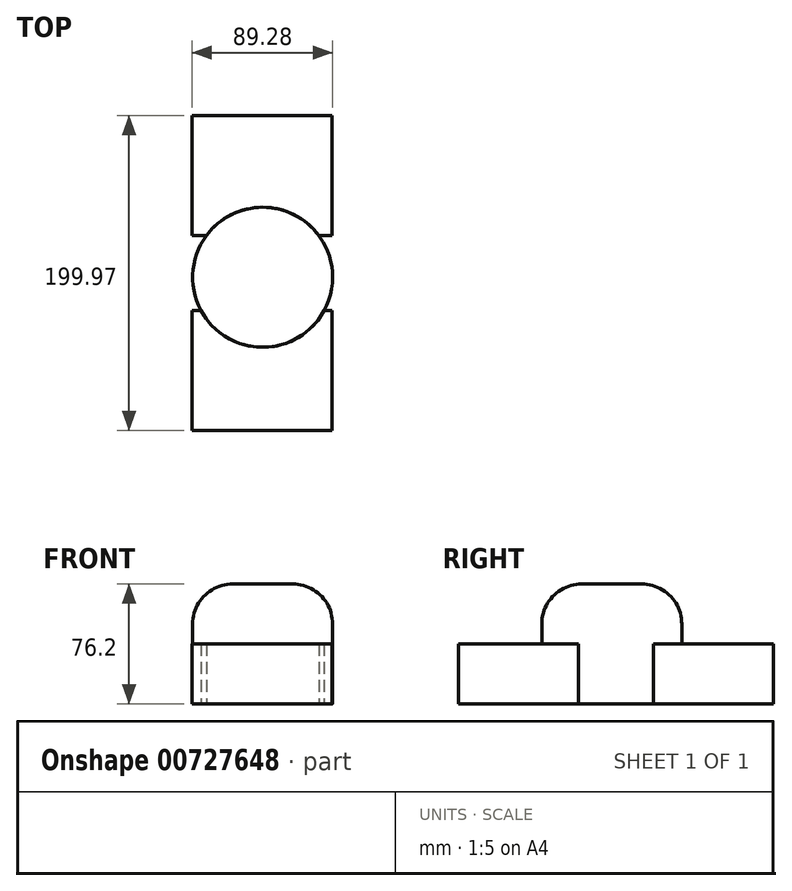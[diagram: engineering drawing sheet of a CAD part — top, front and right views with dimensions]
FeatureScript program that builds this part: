
annotation { "Feature Type Name" : "Feature", "Feature Type Description" : "" }
export const myFeature = defineFeature(function(context is Context, id is Id, definition is map)
    precondition{}
    {
        {
            var Q0;
            Q0=qCreatedBy(makeId("Top.planeOp"),FACE);
            var sketch = newSketch(context, id + "F0", { "sketchPlane" : qUnion([Q0])});
            skCircle(sketch, "E0", {"center": v(0, 21.09) * mm, "radius": 44.45 * mm});
            skSolve(sketch);
        }
        {
            var Q0;
            Q0=makeQuery(id+"F0.imprint","IMPRINT",FACE,{"disambiguationData":[TD([[makeQuery(id+"F0.imprint","IMPRINT",EDGE,{"derivedFrom":sQuery(id+"F0.wireOp",EDGE,"E0")}),1.0]])]});
            var Q1;
            Q1=sQuery(id+"F0.wireOp",EDGE,"E0");
            extrude(context, id + "F1", {"entities" : qUnion([Q0]), "surfaceOperationType" : NewSurfaceOperationType.ADD, "surfaceEntities" : qUnion([Q1]), "depth" : 76.2 * mm, "offsetDistance" : 25.4 * mm});
        }
        {
            var Q0;
            Q0=makeQuery(id+"F1.opExtrude","CAP_EDGE",EDGE,{"disambiguationData":[OSD([sQuery(id+"F0.wireOp",EDGE,"E0")])],"isStart":false});
            fillet(context, id + "F2", {"entities" : qUnion([Q0]), "radius" : 25.4 * mm, "tangentPropagation" : true, "allowEdgeOverflow" : false});
        }
        {
            var Q0;
            Q0=qCreatedBy(makeId("Top.planeOp"),FACE);
            var sketch = newSketch(context, id + "F3", { "sketchPlane" : qUnion([Q0])});
            skLineSegment(sketch, "E1.bottom", {"start": v(-44.83, 0) * mm, "end": v(44.07, 0) * mm});
            skLineSegment(sketch, "E1.top", {"start": v(-44.83, -76.2) * mm, "end": v(44.07, -76.2) * mm});
            skLineSegment(sketch, "E1.left", {"start": v(-44.83, 0) * mm, "end": v(-44.83, -76.2) * mm});
            skLineSegment(sketch, "E1.right", {"start": v(44.07, 0) * mm, "end": v(44.07, -76.2) * mm});
            skLineSegment(sketch, "E2.bottom", {"start": v(44.07, 47.57) * mm, "end": v(-44.83, 47.57) * mm});
            skLineSegment(sketch, "E2.top", {"start": v(44.07, 123.77) * mm, "end": v(-44.83, 123.77) * mm});
            skLineSegment(sketch, "E2.left", {"start": v(44.07, 47.57) * mm, "end": v(44.07, 123.77) * mm});
            skLineSegment(sketch, "E2.right", {"start": v(-44.83, 47.57) * mm, "end": v(-44.83, 123.77) * mm});
            skSolve(sketch);
        }
        {
            var Q0;
            Q0=makeQuery(id+"F3.imprint","IMPRINT",FACE,{"disambiguationData":[TD([[makeQuery(id+"F3.imprint","IMPRINT",EDGE,{"derivedFrom":sQuery(id+"F3.wireOp",EDGE,"E1.bottom")}),-1.0]])]});
            var Q1;
            Q1=makeQuery(id+"F3.imprint","IMPRINT",FACE,{"disambiguationData":[TD([[makeQuery(id+"F3.imprint","IMPRINT",EDGE,{"derivedFrom":sQuery(id+"F3.wireOp",EDGE,"E2.bottom")}),-1.0]])]});
            extrude(context, id + "F4", {"entities" : qUnion([Q0, Q1]), "operationType" : NewBodyOperationType.ADD, "depth" : 38.1 * mm, "offsetDistance" : 25.4 * mm});
        }
    });
